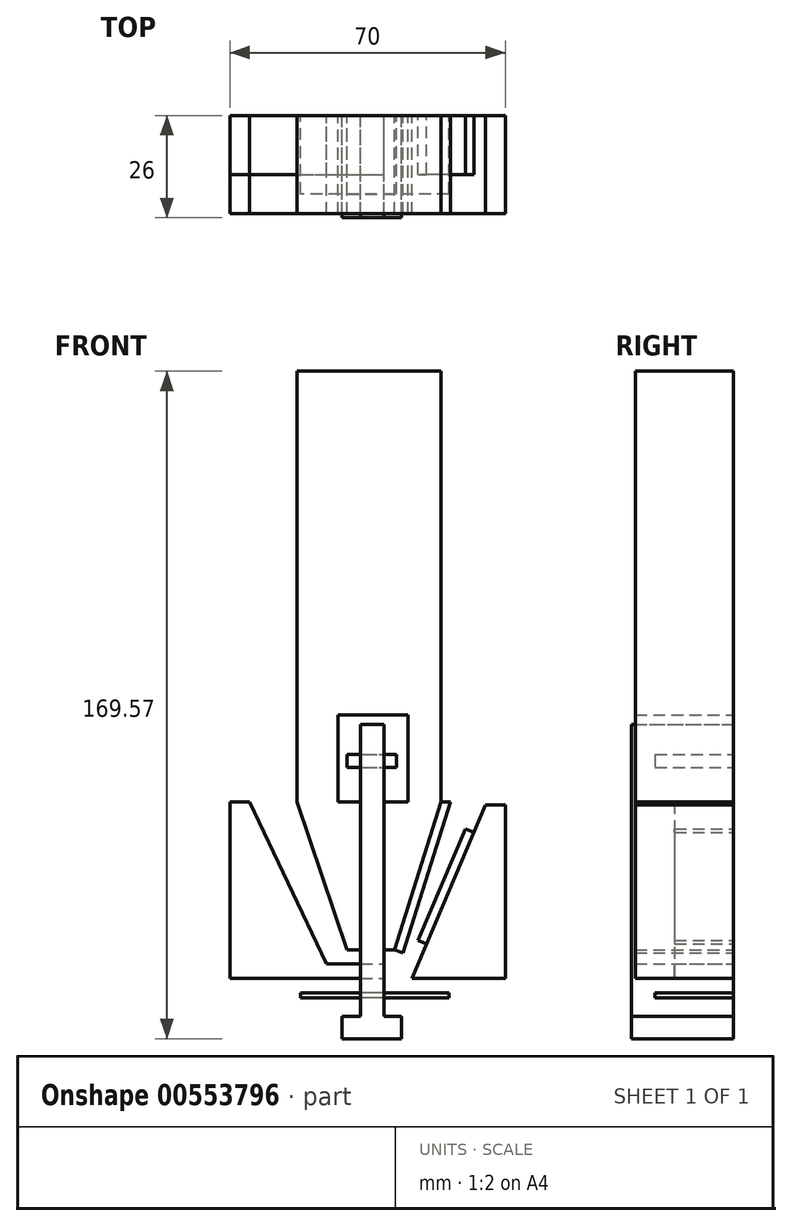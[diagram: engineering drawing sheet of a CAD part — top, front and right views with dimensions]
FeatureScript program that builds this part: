
annotation { "Feature Type Name" : "Feature", "Feature Type Description" : "" }
export const myFeature = defineFeature(function(context is Context, id is Id, definition is map)
    precondition{}
    {
        {
            var Q0;
            Q0=qCreatedBy(makeId("Front.planeOp"),FACE);
            var sketch = newSketch(context, id + "F0", { "sketchPlane" : qUnion([Q0])});
            skLineSegment(sketch, "E0", {"start": v(-31.3, 44.71) * mm, "end": v(-10, 0) * mm});
            skLineSegment(sketch, "E1", {"start": v(28.7, 43.96) * mm, "end": v(10, 0) * mm});
            skLineSegment(sketch, "E2", {"start": v(28.7, 43.96) * mm, "end": v(33.7, 43.96) * mm});
            skLineSegment(sketch, "E3", {"start": v(33.7, 43.96) * mm, "end": v(15, 0) * mm});
            skLineSegment(sketch, "E4", {"start": v(15, 0) * mm, "end": v(10, 0) * mm});
            skLineSegment(sketch, "E5", {"start": v(-31.3, 44.71) * mm, "end": v(-36.3, 44.71) * mm});
            skLineSegment(sketch, "E6", {"start": v(-36.3, 44.71) * mm, "end": v(-15, 0) * mm});
            skLineSegment(sketch, "E7", {"start": v(-15, 0) * mm, "end": v(-10, 0) * mm});
            skLineSegment(sketch, "E8", {"start": v(17.38, 44.71) * mm, "end": v(5.57, 7.19) * mm});
            skLineSegment(sketch, "E9", {"start": v(5.57, 7.19) * mm, "end": v(-6.57, 7.19) * mm});
            skLineSegment(sketch, "E10", {"start": v(-6.57, 7.19) * mm, "end": v(-19.23, 44.71) * mm});
            skLineSegment(sketch, "E11.bottom", {"start": v(-3.04, -9.67) * mm, "end": v(2.92, -9.67) * mm});
            skLineSegment(sketch, "E11.top", {"start": v(-3.04, 64.48) * mm, "end": v(2.92, 64.48) * mm});
            skLineSegment(sketch, "E11.left", {"start": v(-3.04, -9.67) * mm, "end": v(-3.04, 64.48) * mm});
            skLineSegment(sketch, "E11.right", {"start": v(2.92, -9.67) * mm, "end": v(2.92, 64.48) * mm});
            skLineSegment(sketch, "E12.bottom", {"start": v(19.4, -5.07) * mm, "end": v(-18.36, -5.07) * mm});
            skLineSegment(sketch, "E12.top", {"start": v(19.4, -3.72) * mm, "end": v(-18.36, -3.72) * mm});
            skLineSegment(sketch, "E12.left", {"start": v(19.4, -5.07) * mm, "end": v(19.4, -3.72) * mm});
            skLineSegment(sketch, "E12.right", {"start": v(-18.36, -5.07) * mm, "end": v(-18.36, -3.72) * mm});
            skLineSegment(sketch, "E13.bottom", {"start": v(-7.76, -9.67) * mm, "end": v(7.32, -9.67) * mm});
            skLineSegment(sketch, "E13.top", {"start": v(-7.76, -15.38) * mm, "end": v(7.32, -15.38) * mm});
            skLineSegment(sketch, "E13.left", {"start": v(-7.76, -9.67) * mm, "end": v(-7.76, -15.38) * mm});
            skLineSegment(sketch, "E13.right", {"start": v(7.32, -9.67) * mm, "end": v(7.32, -15.38) * mm});
            skLineSegment(sketch, "E14.bottom", {"start": v(-6.48, 56.84) * mm, "end": v(6.1, 56.84) * mm});
            skLineSegment(sketch, "E14.top", {"start": v(-6.48, 53.52) * mm, "end": v(6.1, 53.52) * mm});
            skLineSegment(sketch, "E14.left", {"start": v(-6.48, 56.84) * mm, "end": v(-6.48, 53.52) * mm});
            skLineSegment(sketch, "E14.right", {"start": v(6.1, 56.84) * mm, "end": v(6.1, 53.52) * mm});
            skLineSegment(sketch, "E15", {"start": v(19.76, 44.71) * mm, "end": v(7.7, 6.38) * mm});
            skLineSegment(sketch, "E16", {"start": v(7.7, 6.38) * mm, "end": v(5.57, 7.19) * mm});
            skLineSegment(sketch, "E17", {"start": v(17.38, 44.71) * mm, "end": v(19.76, 44.71) * mm});
            skLineSegment(sketch, "E18", {"start": v(25.74, 37) * mm, "end": v(23.61, 37.9) * mm});
            skLineSegment(sketch, "E19", {"start": v(23.61, 37.9) * mm, "end": v(11.56, 9.56) * mm});
            skLineSegment(sketch, "E20", {"start": v(11.56, 9.56) * mm, "end": v(13.68, 8.66) * mm});
            skLineSegment(sketch, "E21", {"start": v(33.7, 43.96) * mm, "end": v(33.7, 0) * mm});
            skLineSegment(sketch, "E22", {"start": v(33.7, 0) * mm, "end": v(15, 0) * mm});
            skLineSegment(sketch, "E23", {"start": v(-36.3, 44.71) * mm, "end": v(-36.3, 0) * mm});
            skLineSegment(sketch, "E24", {"start": v(-36.3, 0) * mm, "end": v(-15, 0) * mm});
            skLineSegment(sketch, "E25", {"start": v(-19.23, 44.71) * mm, "end": v(-19.23, 154.19) * mm});
            skLineSegment(sketch, "E26", {"start": v(-19.23, 154.19) * mm, "end": v(17.38, 154.19) * mm});
            skLineSegment(sketch, "E27", {"start": v(17.38, 154.19) * mm, "end": v(17.38, 44.71) * mm});
            skLineSegment(sketch, "E28.top", {"start": v(-8.8, 66.87) * mm, "end": v(9.01, 66.87) * mm});
            skLineSegment(sketch, "E28.left", {"start": v(-8.8, 44.71) * mm, "end": v(-8.8, 66.87) * mm});
            skLineSegment(sketch, "E28.right", {"start": v(9.01, 44.71) * mm, "end": v(9.01, 66.87) * mm});
            skLineSegment(sketch, "E29", {"start": v(-8.8, 44.71) * mm, "end": v(9.01, 44.71) * mm});
            skLineSegment(sketch, "E30", {"start": v(-11.72, 3.6) * mm, "end": v(11.53, 3.6) * mm});
            skLineSegment(sketch, "E31", {"start": v(11.53, 3.6) * mm, "end": v(10, 0) * mm});
            skLineSegment(sketch, "E32", {"start": v(-10, 0) * mm, "end": v(10, 0) * mm});
            skSolve(sketch);
        }
        {
            var Q0;
            {var subQ0=sQuery(id+"F0.wireOp",EDGE,"E8");Q0=makeQuery(id+"F0.imprint","IMPRINT",FACE,{"disambiguationData":[TD([[makeQuery(id+"F0.imprint","IMPRINT",EDGE,{"derivedFrom":subQ0}),-1.0]])]});}
            var Q1;
            {var subQ0=sQuery(id+"F0.wireOp",EDGE,"E10");Q1=makeQuery(id+"F0.imprint","IMPRINT",FACE,{"disambiguationData":[TD([[makeQuery(id+"F0.imprint","IMPRINT",EDGE,{"derivedFrom":subQ0}),-1.0]])]});}
            extrude(context, id + "F1", {"entities" : qUnion([Q0, Q1]), "depth" : 25 * mm, "offsetDistance" : 25 * mm});
        }
        {
            var Q0;
            Q0=makeQuery(id+"F0.imprint","IMPRINT",FACE,{"disambiguationData":[TD([[makeQuery(id+"F0.imprint","IMPRINT",EDGE,{"derivedFrom":sQuery(id+"F0.wireOp",EDGE,"E8")}),1.0]])]});
            extrude(context, id + "F2", {"entities" : qUnion([Q0]), "depth" : 25 * mm, "offsetDistance" : 25 * mm});
        }
        {
            var Q0;
            {var subQ0=sQuery(id+"F0.wireOp",EDGE,"E2");Q0=makeQuery(id+"F0.imprint","IMPRINT",FACE,{"disambiguationData":[TD([[makeQuery(id+"F0.imprint","IMPRINT",EDGE,{"derivedFrom":subQ0}),-1.0]])]});}
            var Q1;
            Q1=makeQuery(id+"F0.imprint","IMPRINT",FACE,{"disambiguationData":[TD([[makeQuery(id+"F0.imprint","IMPRINT",EDGE,{"derivedFrom":sQuery(id+"F0.wireOp",EDGE,"E3")}),1.0]])]});
            var Q2;
            {var subQ5=sQuery(id+"F0.wireOp",EDGE,"E31");Q2=makeQuery(id+"F0.imprint","IMPRINT",FACE,{"disambiguationData":[TD([[makeQuery(id+"F0.imprint","IMPRINT",EDGE,{"derivedFrom":subQ5}),-1.0]])]});}
            var Q3;
            {var subQ0=sQuery(id+"F0.wireOp",EDGE,"E32");var subQ1=sQuery(id+"F0.wireOp",EDGE,"E11.left");var subQ2=makeQuery(id+"F0.imprint","INTERSECT",VERTEX,{"derivedFrom":[subQ1,subQ0]});Q3=makeQuery(id+"F0.imprint","IMPRINT",FACE,{"disambiguationData":[TD([[makeQuery(id+"F0.imprint","IMPRINT",EDGE,{"disambiguationData":[TD([[subQ2,-1.0]])],"derivedFrom":subQ1}),-1.0]])]});}
            var Q4;
            {var subQ0=sQuery(id+"F0.wireOp",EDGE,"E32");var subQ5=sQuery(id+"F0.wireOp",EDGE,"E11.left");var subQ7=makeQuery(id+"F0.imprint","INTERSECT",VERTEX,{"derivedFrom":[subQ5,subQ0]});Q4=makeQuery(id+"F0.imprint","IMPRINT",FACE,{"disambiguationData":[TD([[makeQuery(id+"F0.imprint","IMPRINT",EDGE,{"disambiguationData":[TD([[subQ7,-1.0]])],"derivedFrom":subQ5}),1.0]])]});}
            var Q5;
            {var subQ0=sQuery(id+"F0.wireOp",EDGE,"E5");Q5=makeQuery(id+"F0.imprint","IMPRINT",FACE,{"disambiguationData":[TD([[makeQuery(id+"F0.imprint","IMPRINT",EDGE,{"derivedFrom":subQ0}),1.0]])]});}
            var Q6;
            Q6=makeQuery(id+"F0.imprint","IMPRINT",FACE,{"disambiguationData":[TD([[makeQuery(id+"F0.imprint","IMPRINT",EDGE,{"derivedFrom":sQuery(id+"F0.wireOp",EDGE,"E6")}),-1.0]])]});
            extrude(context, id + "F3", {"entities" : qUnion([Q0, Q1, Q2, Q3, Q4, Q5, Q6]), "depth" : 25 * mm, "offsetDistance" : 25 * mm});
        }
        {
            var Q0;
            {var subQ0=sQuery(id+"F0.wireOp",EDGE,"E18");Q0=makeQuery(id+"F0.imprint","IMPRINT",FACE,{"disambiguationData":[TD([[makeQuery(id+"F0.imprint","IMPRINT",EDGE,{"derivedFrom":subQ0}),1.0]])]});}
            var Q1;
            {var subQ0=sQuery(id+"F0.wireOp",EDGE,"E32");var subQ5=sQuery(id+"F0.wireOp",EDGE,"E11.left");var subQ7=makeQuery(id+"F0.imprint","INTERSECT",VERTEX,{"derivedFrom":[subQ5,subQ0]});Q1=makeQuery(id+"F0.imprint","IMPRINT",FACE,{"disambiguationData":[TD([[makeQuery(id+"F0.imprint","IMPRINT",EDGE,{"disambiguationData":[TD([[subQ7,-1.0]])],"derivedFrom":subQ5}),1.0]])]});}
            var Q2;
            {var subQ5=sQuery(id+"F0.wireOp",EDGE,"E31");Q2=makeQuery(id+"F0.imprint","IMPRINT",FACE,{"disambiguationData":[TD([[makeQuery(id+"F0.imprint","IMPRINT",EDGE,{"derivedFrom":subQ5}),-1.0]])]});}
            var Q3;
            {var subQ0=sQuery(id+"F0.wireOp",EDGE,"E32");var subQ1=sQuery(id+"F0.wireOp",EDGE,"E11.left");var subQ2=makeQuery(id+"F0.imprint","INTERSECT",VERTEX,{"derivedFrom":[subQ1,subQ0]});Q3=makeQuery(id+"F0.imprint","IMPRINT",FACE,{"disambiguationData":[TD([[makeQuery(id+"F0.imprint","IMPRINT",EDGE,{"disambiguationData":[TD([[subQ2,-1.0]])],"derivedFrom":subQ1}),-1.0]])]});}
            var Q4;
            {var subQ0=sQuery(id+"F0.wireOp",EDGE,"E5");Q4=makeQuery(id+"F0.imprint","IMPRINT",FACE,{"disambiguationData":[TD([[makeQuery(id+"F0.imprint","IMPRINT",EDGE,{"derivedFrom":subQ0}),1.0]])]});}
            var Q5;
            Q5=makeQuery(id+"F0.imprint","IMPRINT",FACE,{"disambiguationData":[TD([[makeQuery(id+"F0.imprint","IMPRINT",EDGE,{"derivedFrom":sQuery(id+"F0.wireOp",EDGE,"E6")}),-1.0]])]});
            extrude(context, id + "F4", {"entities" : qUnion([Q0, Q1, Q2, Q3, Q4, Q5]), "depth" : 15 * mm, "offsetDistance" : 25 * mm});
        }
        {
            var Q0;
            {var subQ0=sQuery(id+"F0.wireOp",EDGE,"E14.top");var subQ1=sQuery(id+"F0.wireOp",EDGE,"E11.left");var subQ2=makeQuery(id+"F0.imprint","INTERSECT",VERTEX,{"derivedFrom":[subQ1,subQ0]});Q0=makeQuery(id+"F0.imprint","IMPRINT",FACE,{"disambiguationData":[TD([[makeQuery(id+"F0.imprint","IMPRINT",EDGE,{"disambiguationData":[TD([[subQ2,-1.0]])],"derivedFrom":subQ1}),-1.0]])]});}
            var Q1;
            {var subQ0=sQuery(id+"F0.wireOp",EDGE,"E13.bottom");var subQ1=sQuery(id+"F0.wireOp",EDGE,"E11.left");var subQ2=makeQuery(id+"F0.imprint","INTERSECT",VERTEX,{"derivedFrom":[subQ1,subQ0]});Q1=makeQuery(id+"F0.imprint","IMPRINT",FACE,{"disambiguationData":[TD([[makeQuery(id+"F0.imprint","IMPRINT",EDGE,{"disambiguationData":[TD([[subQ2,-1.0]])],"derivedFrom":subQ1}),-1.0]])]});}
            var Q2;
            {var subQ0=sQuery(id+"F0.wireOp",EDGE,"E11.right");var subQ1=sQuery(id+"F0.wireOp",EDGE,"E9");var subQ2=makeQuery(id+"F0.imprint","INTERSECT",VERTEX,{"derivedFrom":[subQ1,subQ0]});Q2=makeQuery(id+"F0.imprint","IMPRINT",FACE,{"disambiguationData":[TD([[makeQuery(id+"F0.imprint","IMPRINT",EDGE,{"disambiguationData":[TD([[subQ2,-1.0]])],"derivedFrom":subQ1}),1.0]])]});}
            var Q3;
            {var subQ0=sQuery(id+"F0.wireOp",EDGE,"E11.top");Q3=makeQuery(id+"F0.imprint","IMPRINT",FACE,{"disambiguationData":[TD([[makeQuery(id+"F0.imprint","IMPRINT",EDGE,{"derivedFrom":subQ0}),-1.0]])]});}
            var Q4;
            Q4=makeQuery(id+"F0.imprint","IMPRINT",FACE,{"disambiguationData":[TD([[makeQuery(id+"F0.imprint","IMPRINT",EDGE,{"derivedFrom":sQuery(id+"F0.wireOp",EDGE,"E13.top")}),1.0]])]});
            var Q5;
            {var subQ0=sQuery(id+"F0.wireOp",EDGE,"E12.bottom");var subQ1=sQuery(id+"F0.wireOp",EDGE,"E11.left");var subQ2=makeQuery(id+"F0.imprint","INTERSECT",VERTEX,{"derivedFrom":[subQ1,subQ0]});Q5=makeQuery(id+"F0.imprint","IMPRINT",FACE,{"disambiguationData":[TD([[makeQuery(id+"F0.imprint","IMPRINT",EDGE,{"disambiguationData":[TD([[subQ2,-1.0]])],"derivedFrom":subQ1}),-1.0]])]});}
            var Q6;
            {var subQ0=sQuery(id+"F0.wireOp",EDGE,"E11.right");var subQ1=sQuery(id+"F0.wireOp",EDGE,"E9");var subQ2=makeQuery(id+"F0.imprint","INTERSECT",VERTEX,{"derivedFrom":[subQ1,subQ0]});Q6=makeQuery(id+"F0.imprint","IMPRINT",FACE,{"disambiguationData":[TD([[makeQuery(id+"F0.imprint","IMPRINT",EDGE,{"disambiguationData":[TD([[subQ2,-1.0]])],"derivedFrom":subQ1}),-1.0]])]});}
            var Q7;
            {var subQ0=sQuery(id+"F0.wireOp",EDGE,"E29");var subQ1=sQuery(id+"F0.wireOp",EDGE,"E11.left");var subQ2=makeQuery(id+"F0.imprint","INTERSECT",VERTEX,{"derivedFrom":[subQ1,subQ0]});Q7=makeQuery(id+"F0.imprint","IMPRINT",FACE,{"disambiguationData":[TD([[makeQuery(id+"F0.imprint","IMPRINT",EDGE,{"disambiguationData":[TD([[subQ2,-1.0]])],"derivedFrom":subQ1}),-1.0]])]});}
            var Q8;
            {var subQ0=sQuery(id+"F0.wireOp",EDGE,"E12.top");var subQ1=sQuery(id+"F0.wireOp",EDGE,"E11.left");var subQ2=makeQuery(id+"F0.imprint","INTERSECT",VERTEX,{"derivedFrom":[subQ1,subQ0]});Q8=makeQuery(id+"F0.imprint","IMPRINT",FACE,{"disambiguationData":[TD([[makeQuery(id+"F0.imprint","IMPRINT",EDGE,{"disambiguationData":[TD([[subQ2,-1.0]])],"derivedFrom":subQ1}),-1.0]])]});}
            var Q9;
            {var subQ0=sQuery(id+"F0.wireOp",EDGE,"E32");var subQ1=sQuery(id+"F0.wireOp",EDGE,"E11.left");var subQ2=makeQuery(id+"F0.imprint","INTERSECT",VERTEX,{"derivedFrom":[subQ1,subQ0]});Q9=makeQuery(id+"F0.imprint","IMPRINT",FACE,{"disambiguationData":[TD([[makeQuery(id+"F0.imprint","IMPRINT",EDGE,{"disambiguationData":[TD([[subQ2,-1.0]])],"derivedFrom":subQ1}),-1.0]])]});}
            extrude(context, id + "F5", {"entities" : qUnion([Q0, Q1, Q2, Q3, Q4, Q5, Q6, Q7, Q8, Q9]), "depth" : 26 * mm, "offsetDistance" : 25 * mm});
        }
        {
            var Q0;
            {var subQ5=sQuery(id+"F0.wireOp",EDGE,"E12.left");Q0=makeQuery(id+"F0.imprint","IMPRINT",FACE,{"disambiguationData":[TD([[makeQuery(id+"F0.imprint","IMPRINT",EDGE,{"derivedFrom":subQ5}),1.0]])]});}
            var Q1;
            {var subQ5=sQuery(id+"F0.wireOp",EDGE,"E12.right");Q1=makeQuery(id+"F0.imprint","IMPRINT",FACE,{"disambiguationData":[TD([[makeQuery(id+"F0.imprint","IMPRINT",EDGE,{"derivedFrom":subQ5}),-1.0]])]});}
            var Q2;
            {var subQ0=sQuery(id+"F0.wireOp",EDGE,"E12.bottom");var subQ1=sQuery(id+"F0.wireOp",EDGE,"E11.left");var subQ2=makeQuery(id+"F0.imprint","INTERSECT",VERTEX,{"derivedFrom":[subQ1,subQ0]});Q2=makeQuery(id+"F0.imprint","IMPRINT",FACE,{"disambiguationData":[TD([[makeQuery(id+"F0.imprint","IMPRINT",EDGE,{"disambiguationData":[TD([[subQ2,-1.0]])],"derivedFrom":subQ1}),-1.0]])]});}
            extrude(context, id + "F6", {"entities" : qUnion([Q0, Q1, Q2]), "depth" : 20 * mm, "offsetDistance" : 25 * mm});
        }
        {
            var Q0;
            {var subQ0=sQuery(id+"F0.wireOp",EDGE,"E14.top");var subQ1=sQuery(id+"F0.wireOp",EDGE,"E11.left");var subQ2=makeQuery(id+"F0.imprint","INTERSECT",VERTEX,{"derivedFrom":[subQ1,subQ0]});Q0=makeQuery(id+"F0.imprint","IMPRINT",FACE,{"disambiguationData":[TD([[makeQuery(id+"F0.imprint","IMPRINT",EDGE,{"disambiguationData":[TD([[subQ2,-1.0]])],"derivedFrom":subQ1}),-1.0]])]});}
            var Q1;
            {var subQ5=sQuery(id+"F0.wireOp",EDGE,"E14.right");Q1=makeQuery(id+"F0.imprint","IMPRINT",FACE,{"disambiguationData":[TD([[makeQuery(id+"F0.imprint","IMPRINT",EDGE,{"derivedFrom":subQ5}),-1.0]])]});}
            var Q2;
            {var subQ5=sQuery(id+"F0.wireOp",EDGE,"E14.left");Q2=makeQuery(id+"F0.imprint","IMPRINT",FACE,{"disambiguationData":[TD([[makeQuery(id+"F0.imprint","IMPRINT",EDGE,{"derivedFrom":subQ5}),1.0]])]});}
            extrude(context, id + "F7", {"entities" : qUnion([Q0, Q1, Q2]), "depth" : 20 * mm, "offsetDistance" : 25 * mm});
        }
    });
